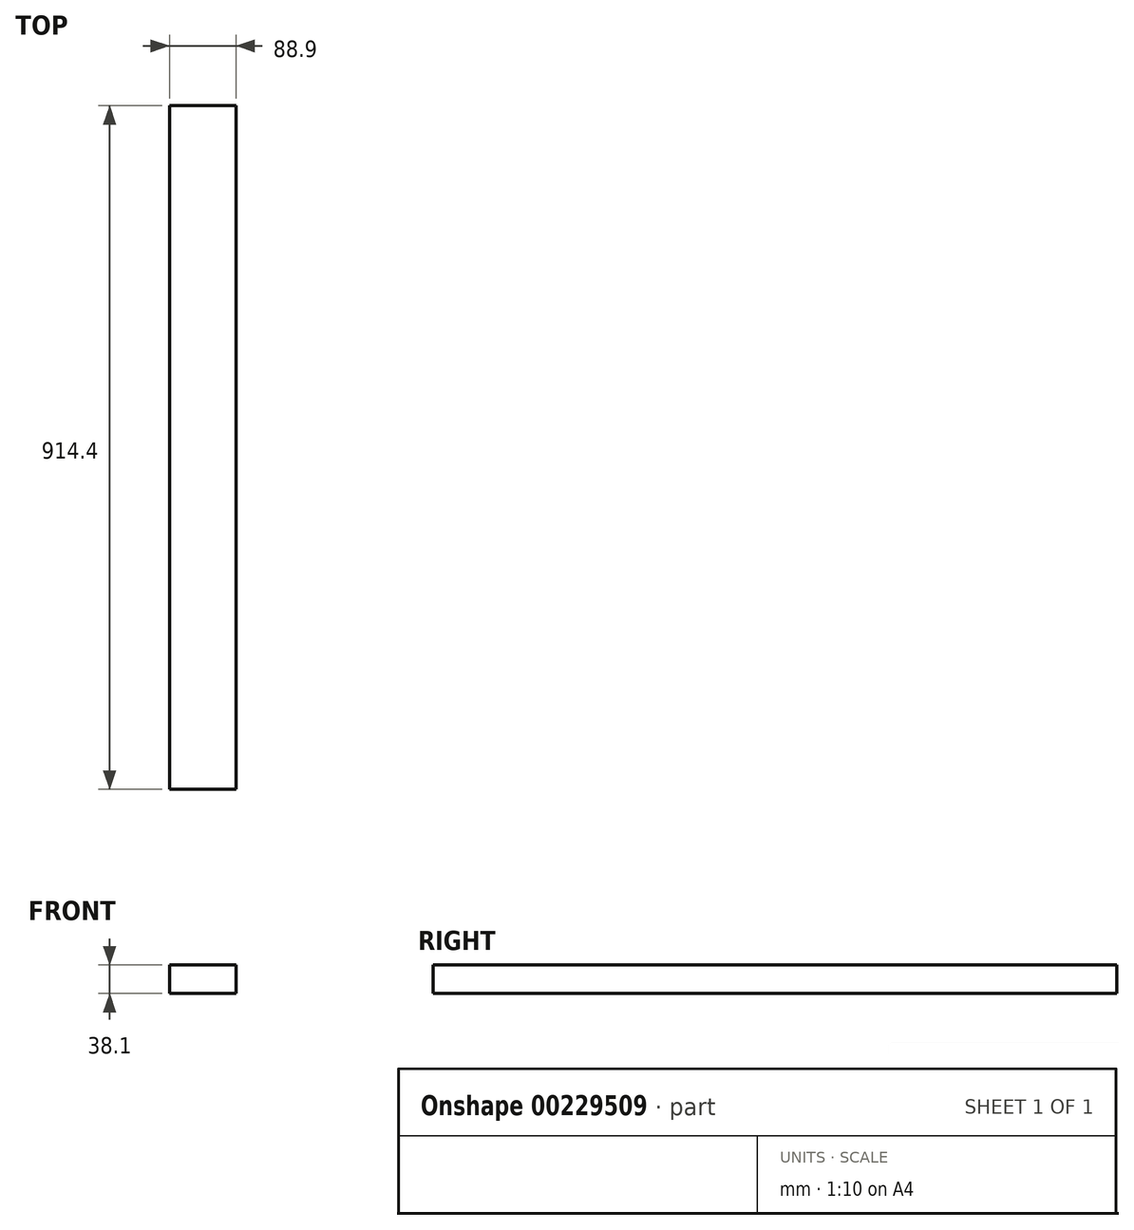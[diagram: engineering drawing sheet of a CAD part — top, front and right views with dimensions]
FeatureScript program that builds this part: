
annotation { "Feature Type Name" : "Feature", "Feature Type Description" : "" }
export const myFeature = defineFeature(function(context is Context, id is Id, definition is map)
    precondition{}
    {
        {
            var Q0;
            Q0=qCreatedBy(makeId("Front.planeOp"),FACE);
            var sketch = newSketch(context, id + "F0", { "sketchPlane" : qUnion([Q0])});
            skLineSegment(sketch, "E0.bottom", {"start": v(0, 0) * mm, "end": v(88.9, 0) * mm});
            skLineSegment(sketch, "E0.top", {"start": v(0, -38.1) * mm, "end": v(88.9, -38.1) * mm});
            skLineSegment(sketch, "E0.left", {"start": v(0, 0) * mm, "end": v(0, -38.1) * mm});
            skLineSegment(sketch, "E0.right", {"start": v(88.9, 0) * mm, "end": v(88.9, -38.1) * mm});
            skSolve(sketch);
        }
        {
            var Q0;
            Q0=qSketchRegion(id+"F0",true);
            extrude(context, id + "F1", {"entities" : qUnion([Q0]), "depth" : 914.4 * mm});
        }
    });
